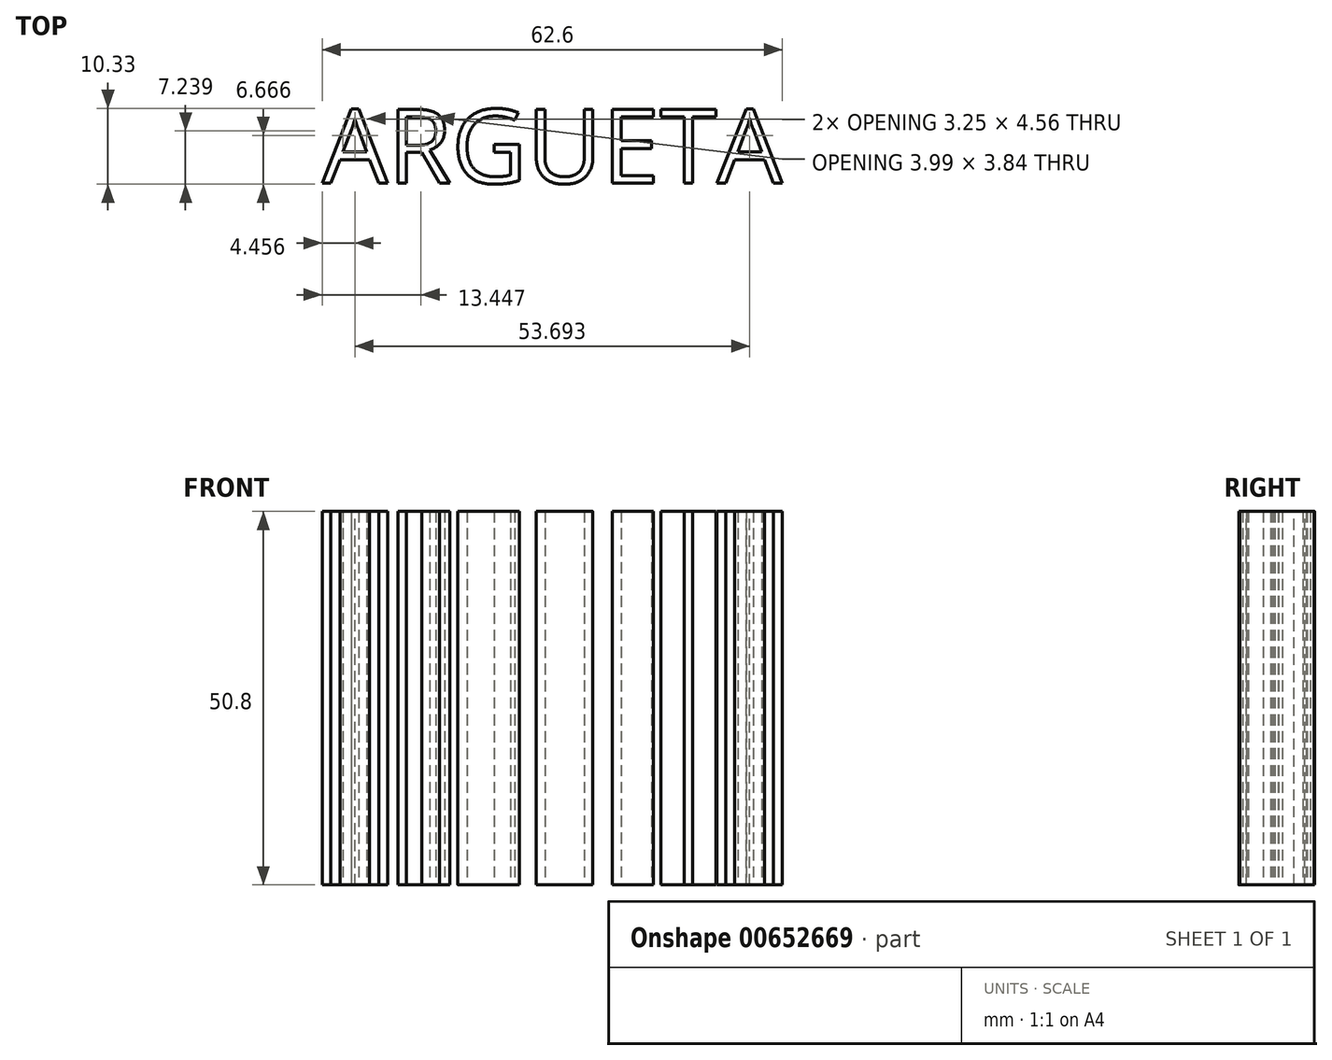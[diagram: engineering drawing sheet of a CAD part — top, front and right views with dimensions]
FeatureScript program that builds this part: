
annotation { "Feature Type Name" : "Feature", "Feature Type Description" : "" }
export const myFeature = defineFeature(function(context is Context, id is Id, definition is map)
    precondition{}
    {
        {
            var Q0;
            Q0=qCreatedBy(makeId("Top.planeOp"),FACE);
            var sketch = newSketch(context, id + "F0", { "sketchPlane" : qUnion([Q0])});
            skText(sketch, "E0", { "text": "ARGUETA\n", "fontName": "OpenSans-Regular.ttf"});
            const initialGuessF0  = {"E0": [-0.02883, -0.00482, 1, 0, 0.01013]};
            skSetInitialGuess(sketch, initialGuessF0);
            skSolve(sketch);
        }
        {
            var Q0;
            Q0 = qSketchRegion(id + "F0", true);
            extrude(context, id + "F1", {"entities" : qUnion([Q0]), "endBound" : BoundingType.SYMMETRIC, "depth" : 50.8 * mm, "offsetDistance" : 25.4 * mm});
        }
    });
